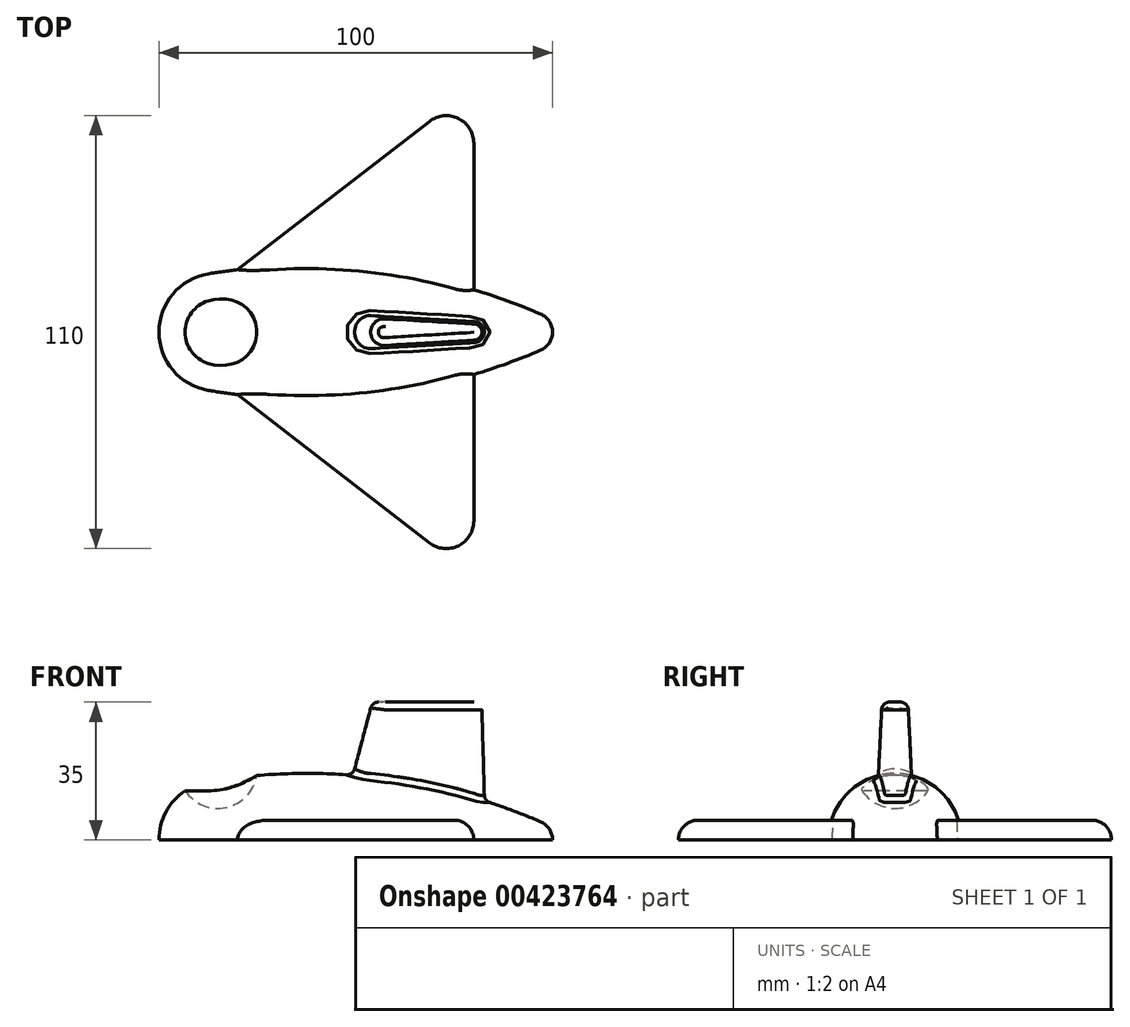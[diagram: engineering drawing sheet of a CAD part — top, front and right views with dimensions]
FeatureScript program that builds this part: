
annotation { "Feature Type Name" : "Feature", "Feature Type Description" : "" }
export const myFeature = defineFeature(function(context is Context, id is Id, definition is map)
    precondition{}
    {
        {
            var Q0;
            Q0=qCreatedBy(makeId("Top.planeOp"),FACE);
            var sketch = newSketch(context, id + "F0", { "sketchPlane" : qUnion([Q0])});
            skArc(sketch, "E0", {"start": v(-2.5, 14.8) * mm, "mid": v(-11.46, 9.68) * mm, "end": v(-15, 0) * mm});
            skArc(sketch, "E1", {"start": v(85, 0) * mm, "mid": v(84.18, 2.75) * mm, "end": v(81.98, 4.6) * mm});
            skArc(sketch, "E2", {"start": v(81.98, 4.6) * mm, "mid": v(40.48, 15.8) * mm, "end": v(-2.5, 14.8) * mm});
            skLineSegment(sketch, "E3", {"start": v(-15, 0) * mm, "end": v(85, 0) * mm});
            skSolve(sketch);
        }
        {
            var Q0;
            Q0=makeQuery(id+"F0.imprint","IMPRINT",FACE,{"disambiguationData":[TD([[makeQuery(id+"F0.imprint","IMPRINT",EDGE,{"derivedFrom":sQuery(id+"F0.wireOp",EDGE,"E0")}),1.0]])]});
            var Q1;
            Q1=sQuery(id+"F0.wireOp",EDGE,"E3");
            revolve(context, id + "F1", {"entities" : qUnion([Q0]), "axis" : qUnion([Q1]), "revolveType" : RevolveType.ONE_DIRECTION, "angle" : 180 * degree});
        }
        {
            var Q0;
            Q0=qCreatedBy(makeId("Front.planeOp"),FACE);
            var sketch = newSketch(context, id + "F2", { "sketchPlane" : qUnion([Q0])});
            skCircle(sketch, "E4", {"center": v(0, 18) * mm, "radius": 10 * mm});
            skArc(sketch, "E5", {"start": v(0, 15) * mm, "mid": v(-10.6, 10.6) * mm, "end": v(-15, 0) * mm});
            skLineSegment(sketch, "E6", {"start": v(0, 18) * mm, "end": v(32.53, 18) * mm});
            skLineSegment(sketch, "E7", {"start": v(0, 18) * mm, "end": v(-29.23, 18) * mm});
            skSolve(sketch);
        }
        {
            var Q0;
            {var subQ0=sQuery(id+"F2.wireOp",EDGE,"E6");var subQ1=sQuery(id+"F2.wireOp",EDGE,"E4");var subQ2=makeQuery(id+"F2.imprint","INTERSECT",VERTEX,{"derivedFrom":[subQ1,subQ0]});Q0=makeQuery(id+"F2.imprint","IMPRINT",FACE,{"disambiguationData":[TD([[makeQuery(id+"F2.imprint","IMPRINT",EDGE,{"disambiguationData":[TD([[subQ2,1.0]])],"derivedFrom":subQ1}),1.0]])]});}
            var Q1;
            Q1=sQuery(id+"F2.wireOp",EDGE,"E7");
            revolve(context, id + "F3", {"operationType" : NewBodyOperationType.REMOVE, "entities" : qUnion([Q0]), "axis" : qUnion([Q1]), "revolveType" : RevolveType.FULL, "oppositeDirection" : true});
        }
        {
            var Q0;
            Q0=qCreatedBy(makeId("Top.planeOp"),FACE);
            var sketch = newSketch(context, id + "F4", { "sketchPlane" : qUnion([Q0])});
            skArc(sketch, "E8", {"start": v(35.33, 4.99) * mm, "mid": v(30, 0) * mm, "end": v(35.33, -4.99) * mm});
            skArc(sketch, "E9", {"start": v(65.2, -3) * mm, "mid": v(68, 0) * mm, "end": v(65.2, 3) * mm});
            skLineSegment(sketch, "E10", {"start": v(35.33, 4.99) * mm, "end": v(65.2, 3) * mm});
            skLineSegment(sketch, "E11.MirrorCS", {"start": v(35.33, -4.99) * mm, "end": v(65.2, -3) * mm});
            skSolve(sketch);
        }
        {
            var Q0;
            Q0=qCreatedBy(makeId("Top.planeOp"),FACE);
            cPlane(context, id + "F5", {"entities" : qUnion([Q0]), "cplaneType" : CPlaneType.OFFSET, "offset" : 35 * mm, "width" : 150 * mm, "height" : 150 * mm});
        }
        {
            var Q0;
            Q0=qCreatedBy(id+"F5.planeOp",FACE);
            var sketch = newSketch(context, id + "F6", { "sketchPlane" : qUnion([Q0])});
            skPoint(sketch, "E12.0", {"position": v(65, 0) * mm});
            skArc(sketch, "E13", {"start": v(65.12, -2) * mm, "mid": v(67, 0) * mm, "end": v(65.12, 2) * mm});
            skArc(sketch, "E14", {"start": v(42.7, 3.3) * mm, "mid": v(39.2, 0) * mm, "end": v(42.7, -3.3) * mm});
            skLineSegment(sketch, "E15", {"start": v(42.7, -3.3) * mm, "end": v(65.12, -2) * mm});
            skLineSegment(sketch, "E16", {"start": v(42.7, 3.3) * mm, "end": v(65.12, 2) * mm});
            skSolve(sketch);
        }
        {
            var Q1;
            Q1 = qSketchRegion(id + "F4", true);
            var Q2;
            Q2 = qSketchRegion(id + "F6", true);
            loft(context, id + "F7", {"operationType" : NewBodyOperationType.ADD, "sheetProfilesArray" : [{ "sheetProfileEntities" : qUnion([Q1]) }, { "sheetProfileEntities" : qUnion([Q2]) }]});
        }
        {
            var Q0;
            Q0=qCreatedBy(makeId("Top.planeOp"),FACE);
            var sketch = newSketch(context, id + "F8", { "sketchPlane" : qUnion([Q0])});
            skArc(sketch, "E17.0", {"start": v(81.98, 4.6) * mm, "mid": v(40.48, 15.8) * mm, "end": v(-2.5, 14.8) * mm, "construction": true});
            skLineSegment(sketch, "E18", {"start": v(5, 15.86) * mm, "end": v(53.72, 53.54) * mm});
            skLineSegment(sketch, "E19", {"start": v(65, 48) * mm, "end": v(65, 10.74) * mm});
            skPoint(sketch, "E20.visualSharp", {"position": v(65, 62.26) * mm});
            skArc(sketch, "E20.filletArc", {"start": v(65, 48) * mm, "mid": v(61.08, 54.28) * mm, "end": v(53.72, 53.54) * mm});
            skLineSegment(sketch, "E21", {"start": v(14.67, 55) * mm, "end": v(103.4, 55) * mm, "construction": true});
            skLineSegment(sketch, "E22", {"start": v(5, 11) * mm, "end": v(65, 6.1) * mm});
            skLineSegment(sketch, "E23", {"start": v(65, 6.1) * mm, "end": v(65, 10.74) * mm});
            skLineSegment(sketch, "E24", {"start": v(5, 15.86) * mm, "end": v(-6.17, 7.23) * mm});
            skLineSegment(sketch, "E25", {"start": v(5, 11) * mm, "end": v(-6.17, 7.23) * mm});
            skSolve(sketch);
        }
        {
            var Q0;
            Q0=makeQuery(id+"F8.imprint","IMPRINT",FACE,{"disambiguationData":[TD([[makeQuery(id+"F8.imprint","IMPRINT",EDGE,{"derivedFrom":sQuery(id+"F8.wireOp",EDGE,"E18")}),-1.0]])]});
            extrude(context, id + "F9", {"entities" : qUnion([Q0]), "operationType" : NewBodyOperationType.ADD, "depth" : 5 * mm});
        }
        {
            var Q0;
            Q0=makeQuery(id+"F1.opRevolve","SWEPT_BODY",BODY,{"disambiguationData":[OSD([sQuery(id+"F0.wireOp",EDGE,"E0"),sQuery(id+"F0.wireOp",EDGE,"E1"),sQuery(id+"F0.wireOp",EDGE,"E2"),sQuery(id+"F0.wireOp",EDGE,"E3")])]});
            var Q1;
            Q1=qCreatedBy(makeId("Front.planeOp"),FACE);
            mirror(context, id + "F10", {"operationType" : NewBodyOperationType.ADD, "entities" : qUnion([Q0]), "mirrorPlane" : qUnion([Q1])});
        }
        {
            var Q0;
            Q0=makeQuery(id+"F10.opPattern","COPY",EDGE,{"derivedFrom":makeQuery(id+"F9.opExtrude","CAP_EDGE",EDGE,{"disambiguationData":[OSD([sQuery(id+"F8.wireOp",EDGE,"E18"),sQuery(id+"F8.wireOp",EDGE,"E24")])],"isStart":false}),"instanceName":"1"});
            var Q1;
            Q1=makeQuery(id+"F9.opExtrude","CAP_EDGE",EDGE,{"disambiguationData":[OSD([sQuery(id+"F8.wireOp",EDGE,"E19"),sQuery(id+"F8.wireOp",EDGE,"E23")])],"isStart":false});
            fillet(context, id + "F11", {"entities" : qUnion([Q0, Q1]), "radius" : 5 * mm, "tangentPropagation" : true, "allowEdgeOverflow" : false});
        }
        {
            var Q0;
            Q0=makeQuery(id+"F7.boolean.opBoolean","INTERSECT",EDGE,{"derivedFrom":[makeQuery(id+"F1.opRevolve","SWEPT_FACE",FACE,{"disambiguationData":[OSD([sQuery(id+"F0.wireOp",EDGE,"E2")])]}),makeQuery(id+"F7.opLoft","SWEPT_FACE",FACE,{"disambiguationData":[OSD([sQuery(id+"F4.wireOp",EDGE,"E8"),sQuery(id+"F4.wireOp",EDGE,"E10"),sQuery(id+"F4.wireOp",EDGE,"E11.MirrorCS"),sQuery(id+"F6.wireOp",EDGE,"E14"),sQuery(id+"F6.wireOp",EDGE,"E15"),sQuery(id+"F6.wireOp",EDGE,"E16")])]})]});
            var Q1;
            Q1=makeQuery(id+"F7.opLoft","MID_CAP_EDGE",EDGE,{"disambiguationData":[OSD([sQuery(id+"F6.wireOp",EDGE,"E14"),sQuery(id+"F6.wireOp",EDGE,"E15"),sQuery(id+"F6.wireOp",EDGE,"E16")])],"capPos":1.0});
            fillet(context, id + "F12", {"entities" : qUnion([Q0, Q1]), "radius" : 2 * mm, "tangentPropagation" : true, "allowEdgeOverflow" : false});
        }
    });
